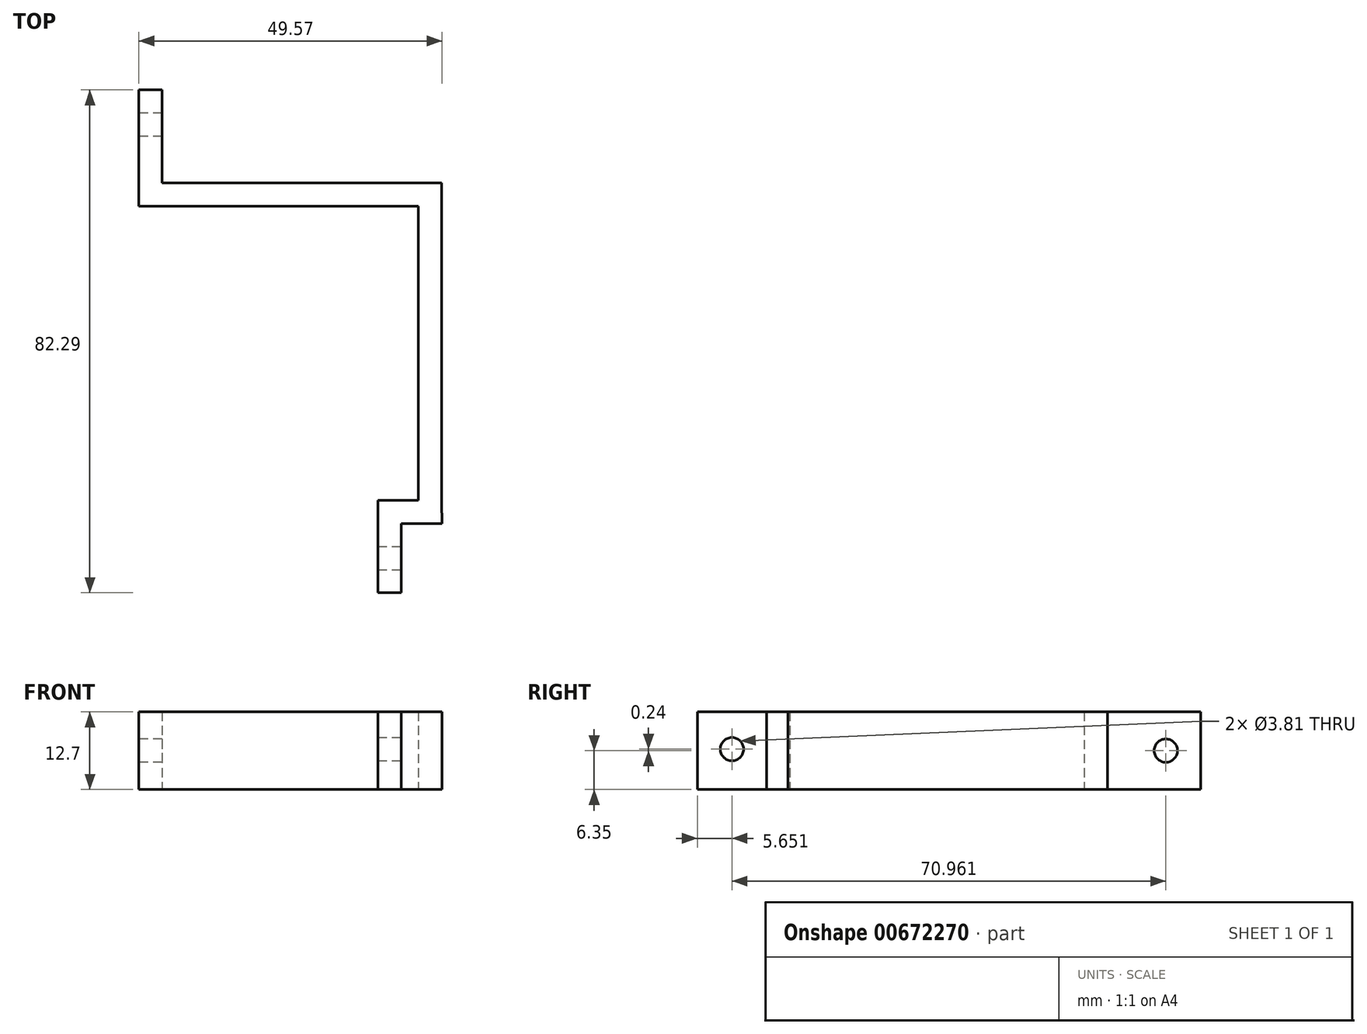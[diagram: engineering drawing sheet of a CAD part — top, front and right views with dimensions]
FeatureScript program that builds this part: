
annotation { "Feature Type Name" : "Feature", "Feature Type Description" : "" }
export const myFeature = defineFeature(function(context is Context, id is Id, definition is map)
    precondition{}
    {
        {
            var Q0;
            Q0=qCreatedBy(makeId("Top.planeOp"),FACE);
            var sketch = newSketch(context, id + "F0", { "sketchPlane" : qUnion([Q0])});
            skLineSegment(sketch, "E0.bottom", {"start": v(-26.78, 16.4) * mm, "end": v(18.94, 16.4) * mm});
            skLineSegment(sketch, "E0.top", {"start": v(-30.6, 12.6) * mm, "end": v(15.13, 12.6) * mm});
            skLineSegment(sketch, "E0.left", {"start": v(-30.6, 16.4) * mm, "end": v(-30.6, 12.6) * mm});
            skLineSegment(sketch, "E0.right", {"start": v(18.94, 16.4) * mm, "end": v(18.94, 12.6) * mm});
            skLineSegment(sketch, "E1.left", {"start": v(18.94, 12.6) * mm, "end": v(18.94, -35.85) * mm});
            skLineSegment(sketch, "E1.right", {"start": v(15.13, 12.6) * mm, "end": v(15.13, -35.54) * mm});
            skLineSegment(sketch, "E2.top", {"start": v(-30.6, 31.64) * mm, "end": v(-26.78, 31.64) * mm});
            skLineSegment(sketch, "E2.left", {"start": v(-30.6, 16.4) * mm, "end": v(-30.6, 31.64) * mm});
            skLineSegment(sketch, "E2.right", {"start": v(-26.78, 16.4) * mm, "end": v(-26.78, 31.64) * mm});
            skPoint(sketch, "E3.right.start.orphan", {"position": v(-0.39, -35.85) * mm});
            skPoint(sketch, "E3.top.end.orphan", {"position": v(-0.39, -51.09) * mm});
            skLineSegment(sketch, "E4", {"start": v(15.13, -35.54) * mm, "end": v(8.47, -35.54) * mm});
            skLineSegment(sketch, "E5", {"start": v(8.47, -35.54) * mm, "end": v(8.47, -39.35) * mm});
            skLineSegment(sketch, "E6", {"start": v(12.28, -39.35) * mm, "end": v(18.98, -39.35) * mm});
            skLineSegment(sketch, "E7", {"start": v(18.98, -39.35) * mm, "end": v(18.94, -35.85) * mm});
            skLineSegment(sketch, "E8", {"start": v(8.47, -39.35) * mm, "end": v(8.47, -50.65) * mm});
            skLineSegment(sketch, "E9", {"start": v(8.47, -50.65) * mm, "end": v(12.28, -50.65) * mm});
            skLineSegment(sketch, "E10", {"start": v(12.28, -50.65) * mm, "end": v(12.28, -39.35) * mm});
            skSolve(sketch);
        }
        {
            var Q0;
            Q0=makeQuery(id+"F0.imprint","IMPRINT",FACE,{"disambiguationData":[TD([[makeQuery(id+"F0.imprint","IMPRINT",EDGE,{"derivedFrom":sQuery(id+"F0.wireOp",EDGE,"E0.bottom")}),-1.0]])]});
            extrude(context, id + "F1", {"entities" : qUnion([Q0]), "depth" : 12.7 * mm, "offsetDistance" : 25.4 * mm});
        }
        {
            var Q0;
            Q0=makeQuery(id+"F1.opExtrude","SWEPT_FACE",FACE,{"disambiguationData":[OSD([sQuery(id+"F0.wireOp",EDGE,"E10")])]});
            var sketch = newSketch(context, id + "F2", { "sketchPlane" : qUnion([Q0])});
            skCircle(sketch, "E11", {"center": v(-45, 6.6) * mm, "radius": 1.9 * mm});
            skPoint(sketch, "E11.centerSnap0", {"position": v(-45, 0) * mm});
            skCircle(sketch, "E12", {"center": v(23.82, 6.38) * mm, "radius": 1.9 * mm});
            skSolve(sketch);
        }
        {
            var Q0;
            Q0=makeQuery(id+"F2.imprint","IMPRINT",FACE,{"disambiguationData":[TD([[makeQuery(id+"F2.imprint","IMPRINT",EDGE,{"derivedFrom":sQuery(id+"F2.wireOp",EDGE,"E11")}),1.0]])]});
            var Q1;
            Q1=sQuery(id+"F2.wireOp",EDGE,"E11");
            extrude(context, id + "F3", {"entities" : qUnion([Q0]), "operationType" : NewBodyOperationType.REMOVE, "surfaceEntities" : qUnion([Q1]), "endBound" : BoundingType.UP_TO_NEXT, "oppositeDirection" : true, "depth" : 25.4 * mm, "offsetDistance" : 25.4 * mm});
        }
        {
            var Q0;
            Q0=makeQuery(id+"F1.opExtrude","SWEPT_FACE",FACE,{"disambiguationData":[OSD([sQuery(id+"F0.wireOp",EDGE,"E0.left"),sQuery(id+"F0.wireOp",EDGE,"E2.left")])]});
            var sketch = newSketch(context, id + "F4", { "sketchPlane" : qUnion([Q0])});
            skCircle(sketch, "E13", {"center": v(-25.96, 6.35) * mm, "radius": 1.9 * mm});
            skPoint(sketch, "E13.centerSnap0", {"position": v(-31.64, 6.35) * mm});
            skSolve(sketch);
        }
        {
            var Q0;
            Q0=makeQuery(id+"F4.imprint","IMPRINT",FACE,{"disambiguationData":[TD([[makeQuery(id+"F4.imprint","IMPRINT",EDGE,{"derivedFrom":sQuery(id+"F4.wireOp",EDGE,"E13")}),1.0]])]});
            var Q1;
            Q1=sQuery(id+"F4.wireOp",EDGE,"E13");
            extrude(context, id + "F5", {"entities" : qUnion([Q0]), "operationType" : NewBodyOperationType.REMOVE, "surfaceEntities" : qUnion([Q1]), "endBound" : BoundingType.UP_TO_NEXT, "oppositeDirection" : true, "depth" : 25.4 * mm, "offsetDistance" : 25.4 * mm});
        }
    });
